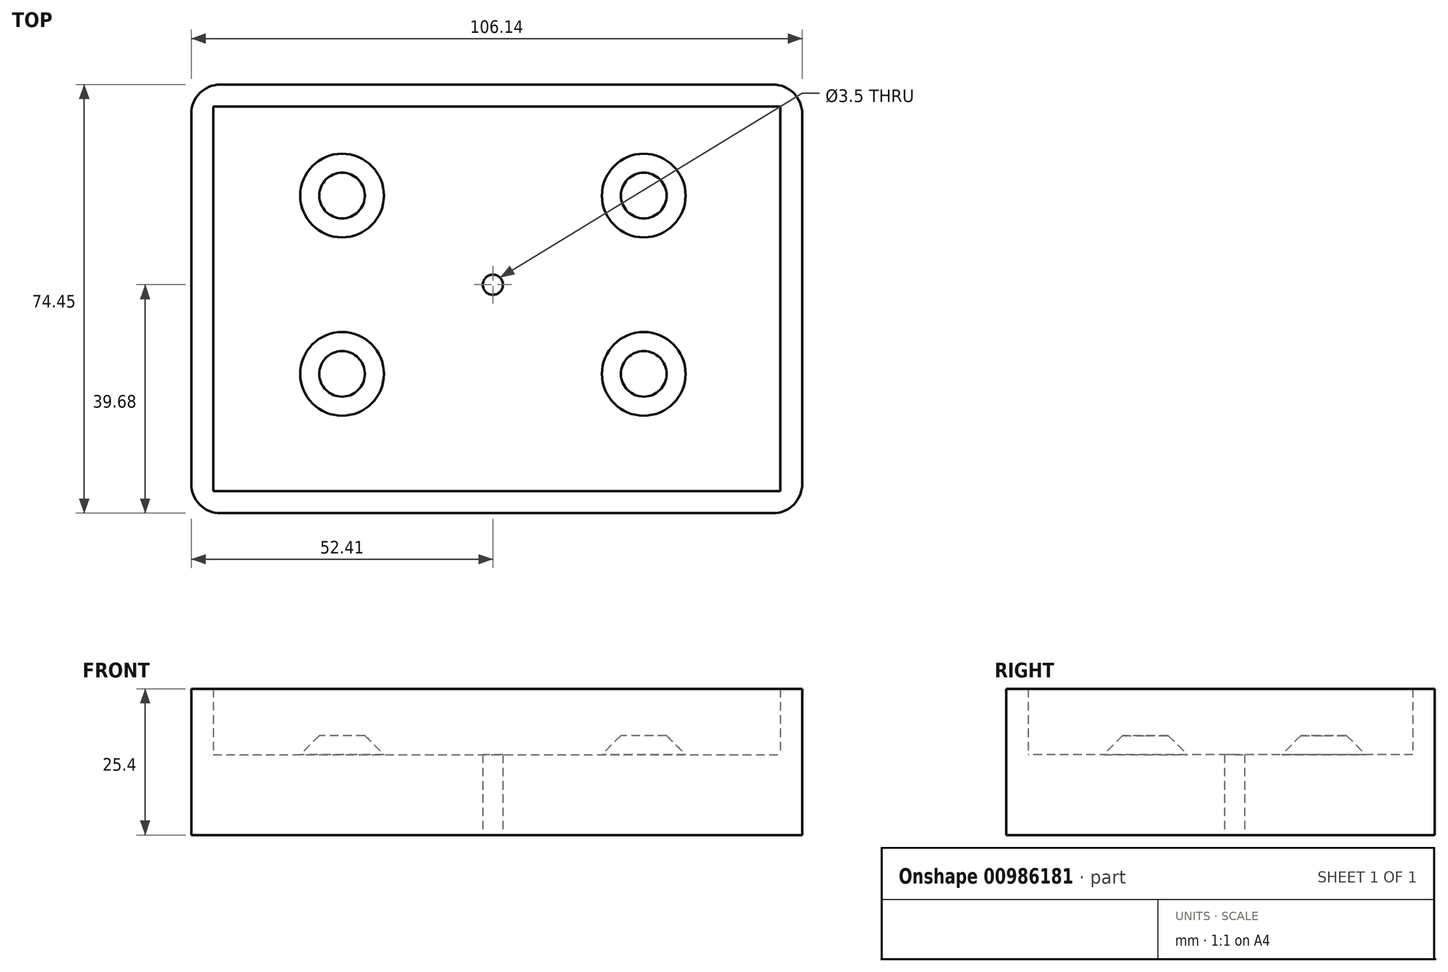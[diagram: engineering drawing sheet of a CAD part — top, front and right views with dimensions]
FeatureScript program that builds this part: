
annotation { "Feature Type Name" : "Feature", "Feature Type Description" : "" }
export const myFeature = defineFeature(function(context is Context, id is Id, definition is map)
    precondition{}
    {
        {
            var Q0;
            Q0=qCreatedBy(makeId("Top.planeOp"),FACE);
            var sketch = newSketch(context, id + "F0", { "sketchPlane" : qUnion([Q0])});
            skLineSegment(sketch, "E0.bottom", {"start": v(-48.6, 30.96) * mm, "end": v(49.92, 30.96) * mm});
            skLineSegment(sketch, "E0.top", {"start": v(-48.6, -35.87) * mm, "end": v(49.92, -35.87) * mm});
            skLineSegment(sketch, "E0.left", {"start": v(-48.6, 30.96) * mm, "end": v(-48.6, -35.87) * mm});
            skLineSegment(sketch, "E0.right", {"start": v(49.92, 30.96) * mm, "end": v(49.92, -35.87) * mm});
            skLineSegment(sketch, "E1.0", {"start": v(-52.4, 34.77) * mm, "end": v(53.73, 34.77) * mm});
            skLineSegment(sketch, "E1.1", {"start": v(-52.4, 34.77) * mm, "end": v(-52.4, -39.68) * mm});
            skLineSegment(sketch, "E1.2", {"start": v(-52.4, -39.68) * mm, "end": v(53.73, -39.68) * mm});
            skLineSegment(sketch, "E1.3", {"start": v(53.73, 34.77) * mm, "end": v(53.73, -39.68) * mm});
            skLineSegment(sketch, "E2.bottom", {"start": v(26.2, -15.49) * mm, "end": v(-26.2, -15.49) * mm, "construction": true});
            skLineSegment(sketch, "E2.top", {"start": v(26.2, 15.49) * mm, "end": v(-26.2, 15.49) * mm, "construction": true});
            skLineSegment(sketch, "E2.left", {"start": v(26.2, -15.49) * mm, "end": v(26.2, 15.49) * mm, "construction": true});
            skLineSegment(sketch, "E2.right", {"start": v(-26.2, -15.49) * mm, "end": v(-26.2, 15.49) * mm, "construction": true});
            skPoint(sketch, "E2.middle", {"position": v(0, 0) * mm});
            skCircle(sketch, "E3", {"center": v(-26.2, 15.49) * mm, "radius": 9.04 * mm});
            skCircle(sketch, "E4", {"center": v(-26.2, -15.49) * mm, "radius": 9.04 * mm});
            skCircle(sketch, "E5", {"center": v(26.2, -15.49) * mm, "radius": 9.04 * mm});
            skCircle(sketch, "E6", {"center": v(26.2, 15.49) * mm, "radius": 9.04 * mm});
            skSolve(sketch);
        }
        {
            var Q0;
            Q0=makeQuery(id+"F0.imprint","IMPRINT",FACE,{"disambiguationData":[TD([[makeQuery(id+"F0.imprint","IMPRINT",EDGE,{"derivedFrom":sQuery(id+"F0.wireOp",EDGE,"E0.bottom")}),1.0]])]});
            extrude(context, id + "F1", {"entities" : qUnion([Q0]), "depth" : 25.4 * mm, "offsetDistance" : 25.4 * mm});
        }
        {
            var Q0;
            Q0=makeQuery(id+"F0.imprint","IMPRINT",FACE,{"disambiguationData":[TD([[makeQuery(id+"F0.imprint","IMPRINT",EDGE,{"derivedFrom":sQuery(id+"F0.wireOp",EDGE,"E0.bottom")}),-1.0]])]});
            extrude(context, id + "F2", {"entities" : qUnion([Q0]), "operationType" : NewBodyOperationType.ADD, "depth" : 13.97 * mm, "offsetDistance" : 25.4 * mm});
        }
        {
            var Q0;
            Q0=makeQuery(id+"F0.imprint","IMPRINT",FACE,{"disambiguationData":[TD([[makeQuery(id+"F0.imprint","IMPRINT",EDGE,{"derivedFrom":sQuery(id+"F0.wireOp",EDGE,"E4")}),1.0]])]});
            var Q1;
            Q1=makeQuery(id+"F0.imprint","IMPRINT",FACE,{"disambiguationData":[TD([[makeQuery(id+"F0.imprint","IMPRINT",EDGE,{"derivedFrom":sQuery(id+"F0.wireOp",EDGE,"E3")}),1.0]])]});
            var Q2;
            Q2=makeQuery(id+"F0.imprint","IMPRINT",FACE,{"disambiguationData":[TD([[makeQuery(id+"F0.imprint","IMPRINT",EDGE,{"derivedFrom":sQuery(id+"F0.wireOp",EDGE,"E6")}),1.0]])]});
            var Q3;
            Q3=makeQuery(id+"F0.imprint","IMPRINT",FACE,{"disambiguationData":[TD([[makeQuery(id+"F0.imprint","IMPRINT",EDGE,{"derivedFrom":sQuery(id+"F0.wireOp",EDGE,"E5")}),1.0]])]});
            var Q4;
            Q4=sQuery(id+"F0.wireOp",EDGE,"E3");
            var Q5;
            Q5=sQuery(id+"F0.wireOp",EDGE,"E4");
            var Q6;
            Q6=sQuery(id+"F0.wireOp",EDGE,"E5");
            var Q7;
            Q7=sQuery(id+"F0.wireOp",EDGE,"E6");
            extrude(context, id + "F3", {"entities" : qUnion([Q0, Q1, Q2, Q3]), "operationType" : NewBodyOperationType.ADD, "surfaceEntities" : qUnion([Q4, Q5, Q6, Q7]), "depth" : 17.27 * mm, "offsetDistance" : 25.4 * mm});
        }
        {
            var Q0;
            Q0=sQuery(id+"F0.wireOp",VERTEX,"E2.middle");
            var Q1;
            Q1=makeQuery(id+"F1.opExtrude","SWEPT_BODY",BODY,{"disambiguationData":[OSD([sQuery(id+"F0.wireOp",EDGE,"E0.bottom"),sQuery(id+"F0.wireOp",EDGE,"E0.top"),sQuery(id+"F0.wireOp",EDGE,"E0.left"),sQuery(id+"F0.wireOp",EDGE,"E0.right"),sQuery(id+"F0.wireOp",EDGE,"E1.0"),sQuery(id+"F0.wireOp",EDGE,"E1.1"),sQuery(id+"F0.wireOp",EDGE,"E1.2"),sQuery(id+"F0.wireOp",EDGE,"E1.3")])]});
            hole(context, id + "F4", {"style" : HoleStyle.SIMPLE, "endStyle" : HoleEndStyle.THROUGH, "oppositeDirection" : true, "holeDiameter" : 3.5 * mm, "majorDiameter" : 6.35 * mm, "isTappedThrough" : true, "tappedDepth" : 12.7 * mm, "tapClearance" : 3, "locations" : qUnion([Q0]), "scope" : qUnion([Q1])});
        }
        {
            var Q0;
            Q0=makeQuery(id+"F3.opExtrude","CAP_FACE",FACE,{"disambiguationData":[OSD([sQuery(id+"F0.wireOp",EDGE,"E3")])],"isStart":false});
            var Q1;
            Q1=makeQuery(id+"F3.opExtrude","CAP_FACE",FACE,{"disambiguationData":[OSD([sQuery(id+"F0.wireOp",EDGE,"E6")])],"isStart":false});
            var Q2;
            Q2=makeQuery(id+"F3.opExtrude","CAP_FACE",FACE,{"disambiguationData":[OSD([sQuery(id+"F0.wireOp",EDGE,"E5")])],"isStart":false});
            var Q3;
            Q3=makeQuery(id+"F3.opExtrude","CAP_FACE",FACE,{"disambiguationData":[OSD([sQuery(id+"F0.wireOp",EDGE,"E4")])],"isStart":false});
            chamfer(context, id + "F5", {"entities" : qUnion([Q0, Q1, Q2, Q3]), "width" : 5.08 * mm, "tangentPropagation" : true});
        }
        {
            var Q0;
            Q0=makeQuery(id+"F1.opExtrude","SWEPT_EDGE",EDGE,{"disambiguationData":[OSD([sQuery(id+"F0.wireOp",EDGE,"E1.1"),sQuery(id+"F0.wireOp",EDGE,"E1.2")])]});
            var Q1;
            Q1=makeQuery(id+"F1.opExtrude","SWEPT_EDGE",EDGE,{"disambiguationData":[OSD([sQuery(id+"F0.wireOp",EDGE,"E1.0"),sQuery(id+"F0.wireOp",EDGE,"E1.1")])]});
            var Q2;
            Q2=makeQuery(id+"F1.opExtrude","SWEPT_EDGE",EDGE,{"disambiguationData":[OSD([sQuery(id+"F0.wireOp",EDGE,"E1.2"),sQuery(id+"F0.wireOp",EDGE,"E1.3")])]});
            var Q3;
            Q3=makeQuery(id+"F1.opExtrude","SWEPT_EDGE",EDGE,{"disambiguationData":[OSD([sQuery(id+"F0.wireOp",EDGE,"E1.0"),sQuery(id+"F0.wireOp",EDGE,"E1.3")])]});
            fillet(context, id + "F6", {"entities" : qUnion([Q0, Q1, Q2, Q3]), "radius" : 5.08 * mm, "tangentPropagation" : true, "allowEdgeOverflow" : false});
        }
    });
